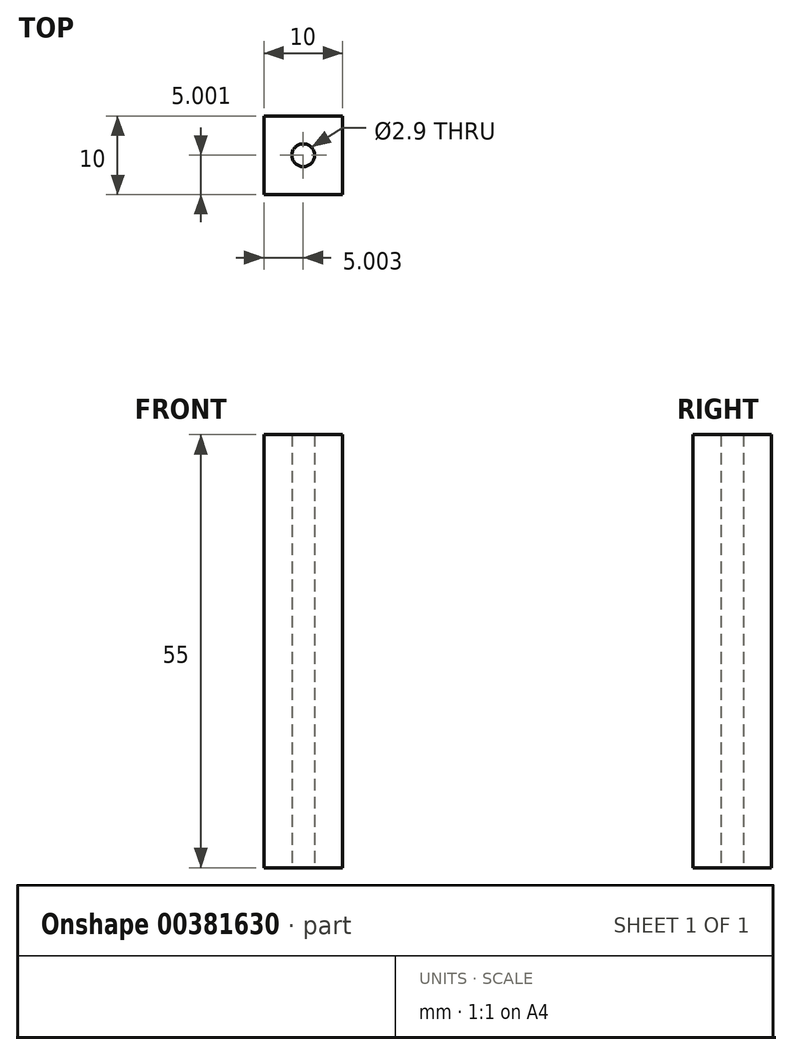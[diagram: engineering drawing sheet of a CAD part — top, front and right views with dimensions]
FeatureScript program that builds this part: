
annotation { "Feature Type Name" : "Feature", "Feature Type Description" : "" }
export const myFeature = defineFeature(function(context is Context, id is Id, definition is map)
    precondition{}
    {
        {
            var Q0;
            Q0=qCreatedBy(makeId("Top.planeOp"),FACE);
            var sketch = newSketch(context, id + "F0", { "sketchPlane" : qUnion([Q0])});
            skLineSegment(sketch, "E0.bottom", {"start": v(-6.79, -5.66) * mm, "end": v(3.21, -5.66) * mm});
            skLineSegment(sketch, "E0.top", {"start": v(-6.79, 4.34) * mm, "end": v(3.21, 4.34) * mm});
            skLineSegment(sketch, "E0.left", {"start": v(-6.79, -5.66) * mm, "end": v(-6.79, 4.34) * mm});
            skLineSegment(sketch, "E0.right", {"start": v(3.21, -5.66) * mm, "end": v(3.21, 4.34) * mm});
            skLineSegment(sketch, "E1", {"start": v(-1.79, 4.34) * mm, "end": v(-1.79, -5.66) * mm, "construction": true});
            skLineSegment(sketch, "E2", {"start": v(-6.79, -0.66) * mm, "end": v(3.21, -0.66) * mm, "construction": true});
            skCircle(sketch, "E3", {"center": v(-1.79, -0.66) * mm, "radius": 1.45 * mm});
            skSolve(sketch);
        }
        {
            var Q0;
            Q0=makeQuery(id+"F0.imprint","IMPRINT",FACE,{"disambiguationData":[TD([[makeQuery(id+"F0.imprint","IMPRINT",EDGE,{"derivedFrom":sQuery(id+"F0.wireOp",EDGE,"E0.bottom")}),1.0]])]});
            extrude(context, id + "F1", {"entities" : qUnion([Q0]), "depth" : 55 * mm, "offsetDistance" : 25 * mm});
        }
    });
